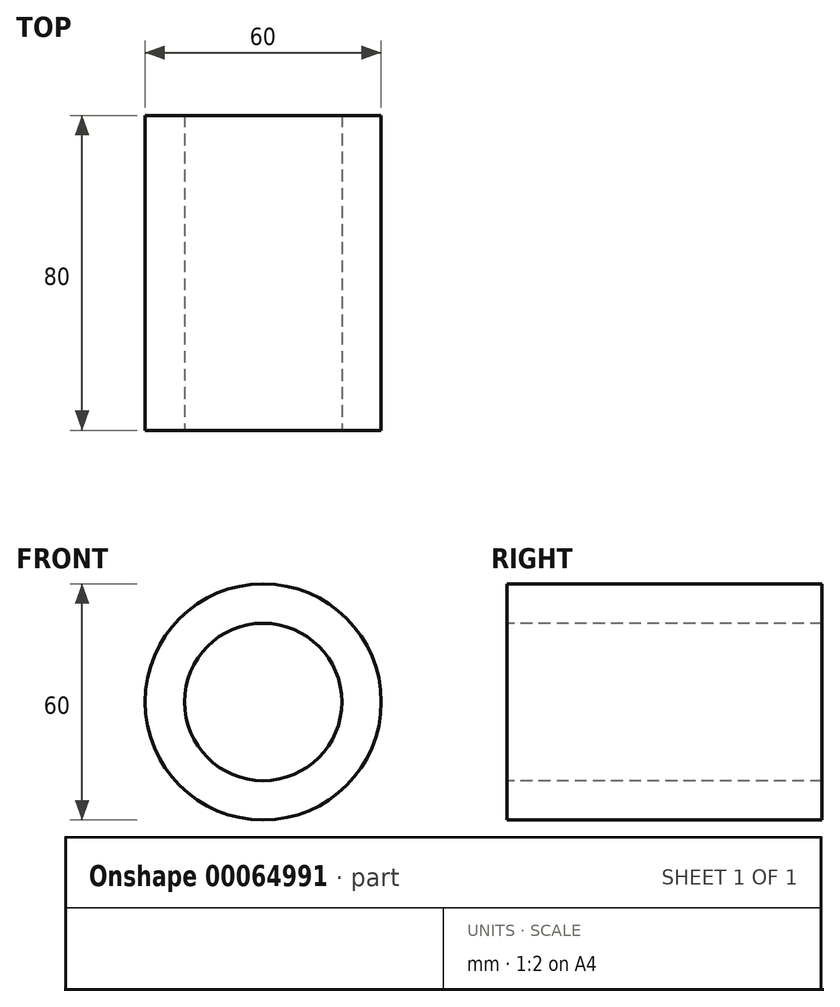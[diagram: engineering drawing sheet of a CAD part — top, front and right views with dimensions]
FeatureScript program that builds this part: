
annotation { "Feature Type Name" : "Feature", "Feature Type Description" : "" }
export const myFeature = defineFeature(function(context is Context, id is Id, definition is map)
    precondition{}
    {
        {
            var Q0;
            Q0=qCreatedBy(makeId("Front.planeOp"),FACE);
            var sketch = newSketch(context, id + "F0", { "sketchPlane" : qUnion([Q0])});
            skCircle(sketch, "E0", {"center": v(0, 0) * mm, "radius": 20 * mm});
            skCircle(sketch, "E1", {"center": v(0, 0) * mm, "radius": 30 * mm});
            skSolve(sketch);
        }
        {
            var Q0;
            Q0=sQuery(id+"F0.wireOp",EDGE,"E0");
            var Q1;
            Q1=sQuery(id+"F0.wireOp",EDGE,"E1");
            extrude(context, id + "F1", {"bodyType" : ToolBodyType.SURFACE, "surfaceEntities" : qUnion([Q0, Q1]), "depth" : 80 * mm});
        }
    });
